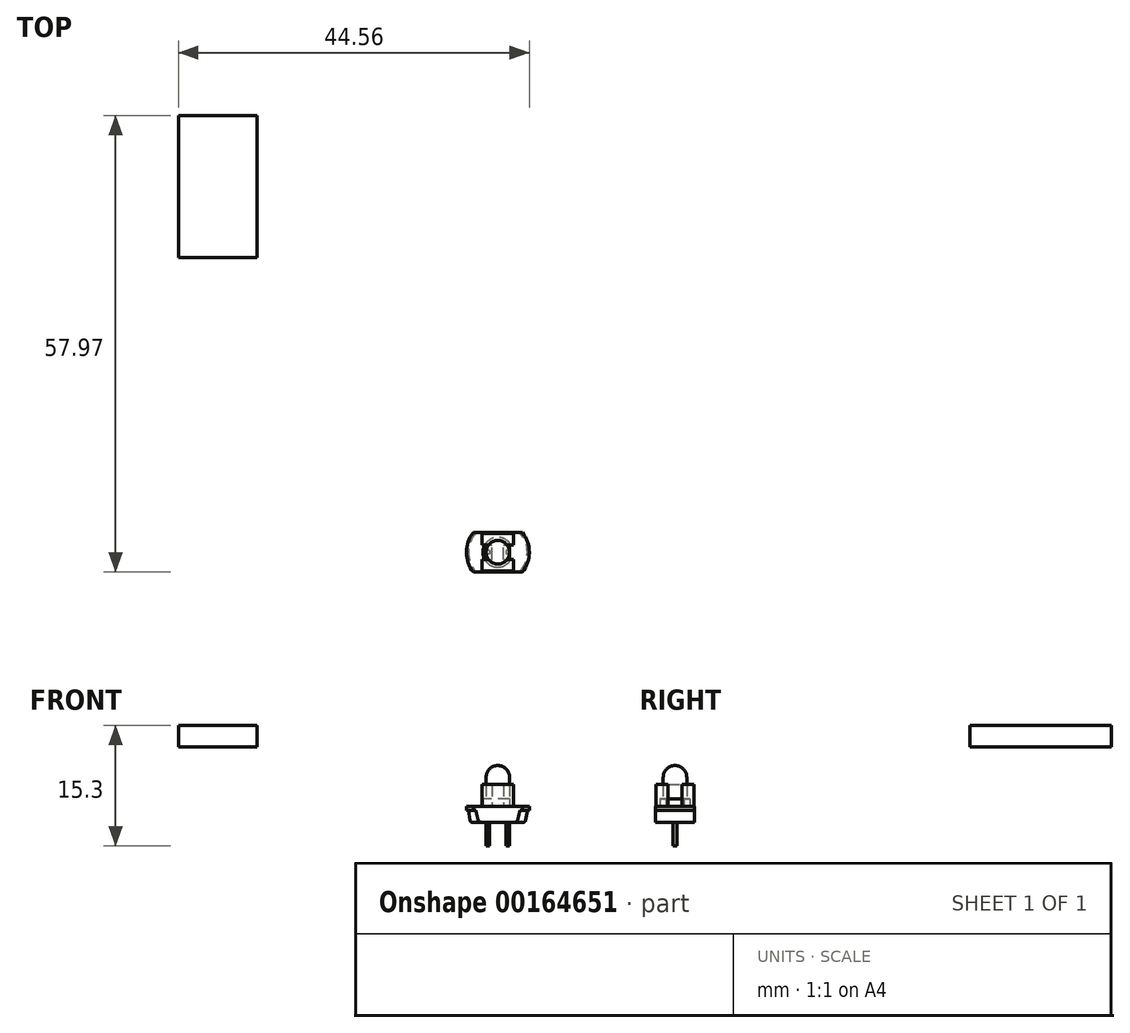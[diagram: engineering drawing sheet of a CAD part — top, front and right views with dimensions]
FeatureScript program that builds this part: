
annotation { "Feature Type Name" : "Feature", "Feature Type Description" : "" }
export const myFeature = defineFeature(function(context is Context, id is Id, definition is map)
    precondition{}
    {
        {
            var Q0;
            Q0=qCreatedBy(makeId("Front.planeOp"),FACE);
            var sketch = newSketch(context, id + "F0", { "sketchPlane" : qUnion([Q0])});
            skLineSegment(sketch, "E0", {"start": v(0, 10.98) * mm, "end": v(0, -8.22) * mm, "construction": true});
            skSolve(sketch);
        }
        {
            var Q0;
            Q0=qCreatedBy(makeId("Top.planeOp"),FACE);
            cPlane(context, id + "F1", {"entities" : qUnion([Q0]), "cplaneType" : CPlaneType.OFFSET, "offset" : 2 * mm, "width" : 150 * mm, "height" : 150 * mm});
        }
        {
            var Q0;
            Q0=qCreatedBy(makeId("Top.planeOp"),FACE);
            var sketch = newSketch(context, id + "F2", { "sketchPlane" : qUnion([Q0])});
            skLineSegment(sketch, "E1", {"start": v(0, 8.57) * mm, "end": v(0, -6.8) * mm, "construction": true});
            skLineSegment(sketch, "E2", {"start": v(-7.73, 0) * mm, "end": v(6.61, 0) * mm, "construction": true});
            skLineSegment(sketch, "E3.bottom", {"start": v(-4.25, 1.75) * mm, "end": v(4.25, 1.75) * mm});
            skLineSegment(sketch, "E3.top", {"start": v(-4.25, -1.75) * mm, "end": v(4.25, -1.75) * mm});
            skLineSegment(sketch, "E3.left", {"start": v(-4.25, 1.75) * mm, "end": v(-4.25, -1.75) * mm});
            skLineSegment(sketch, "E3.right", {"start": v(4.25, 1.75) * mm, "end": v(4.25, -1.75) * mm});
            skSolve(sketch);
        }
        {
            var Q0;
            Q0=qSketchRegion(id+"F2",true);
            extrude(context, id + "F3", {"entities" : qUnion([Q0]), "depth" : 3.5 * mm});
        }
        {
            var Q0;
            Q0=makeQuery(id+"F3.opExtrude","CAP_FACE",FACE,{"disambiguationData":[OSD([sQuery(id+"F2.wireOp",EDGE,"E3.bottom"),sQuery(id+"F2.wireOp",EDGE,"E3.top"),sQuery(id+"F2.wireOp",EDGE,"E3.left"),sQuery(id+"F2.wireOp",EDGE,"E3.right")])],"isStart":false});
            var sketch = newSketch(context, id + "F4", { "sketchPlane" : qUnion([Q0])});
            skLineSegment(sketch, "E4.bottom", {"start": v(-1.75, 0.75) * mm, "end": v(-0.25, 0.75) * mm});
            skLineSegment(sketch, "E4.top", {"start": v(-1.75, -0.75) * mm, "end": v(-0.25, -0.75) * mm});
            skLineSegment(sketch, "E4.left", {"start": v(-1.75, 0.75) * mm, "end": v(-1.75, -0.75) * mm});
            skLineSegment(sketch, "E4.right", {"start": v(-0.25, 0.75) * mm, "end": v(-0.25, -0.75) * mm});
            skLineSegment(sketch, "E5", {"start": v(-2.91, 0) * mm, "end": v(1.63, 0) * mm, "construction": true});
            skSolve(sketch);
        }
        {
            var Q0;
            Q0=qSketchRegion(id+"F4",true);
            extrude(context, id + "F5", {"entities" : qUnion([Q0]), "operationType" : NewBodyOperationType.ADD, "depth" : 2 * mm});
        }
        {
            var Q0;
            Q0=makeQuery(id+"F3.opExtrude","CAP_FACE",FACE,{"disambiguationData":[OSD([sQuery(id+"F2.wireOp",EDGE,"E3.bottom"),sQuery(id+"F2.wireOp",EDGE,"E3.top"),sQuery(id+"F2.wireOp",EDGE,"E3.left"),sQuery(id+"F2.wireOp",EDGE,"E3.right")])],"isStart":true});
            var sketch = newSketch(context, id + "F6", { "sketchPlane" : qUnion([Q0])});
            skLineSegment(sketch, "E6.bottom", {"start": v(-2.8, 2.5) * mm, "end": v(-2.2, 2.5) * mm});
            skLineSegment(sketch, "E6.top", {"start": v(-2.8, 1.75) * mm, "end": v(-2.2, 1.75) * mm});
            skLineSegment(sketch, "E6.left", {"start": v(-2.8, 2.5) * mm, "end": v(-2.8, 1.75) * mm});
            skLineSegment(sketch, "E6.right", {"start": v(-2.2, 2.5) * mm, "end": v(-2.2, 1.75) * mm});
            skLineSegment(sketch, "E7.1.0.0", {"start": v(-0.3, 1.75) * mm, "end": v(0.3, 1.75) * mm});
            skLineSegment(sketch, "E7.1.0.1", {"start": v(-0.3, 2.5) * mm, "end": v(-0.3, 1.75) * mm});
            skLineSegment(sketch, "E7.1.0.2", {"start": v(0.3, 2.5) * mm, "end": v(0.3, 1.75) * mm});
            skLineSegment(sketch, "E7.1.0.3", {"start": v(-0.3, 2.5) * mm, "end": v(0.3, 2.5) * mm});
            skLineSegment(sketch, "E7.2.0.0", {"start": v(2.2, 1.75) * mm, "end": v(2.8, 1.75) * mm});
            skLineSegment(sketch, "E7.2.0.1", {"start": v(2.2, 2.5) * mm, "end": v(2.2, 1.75) * mm});
            skLineSegment(sketch, "E7.2.0.2", {"start": v(2.8, 2.5) * mm, "end": v(2.8, 1.75) * mm});
            skLineSegment(sketch, "E7.2.0.3", {"start": v(2.2, 2.5) * mm, "end": v(2.8, 2.5) * mm});
            skLineSegment(sketch, "E7.direction1", {"start": v(-2.8, 1.75) * mm, "end": v(-0.3, 1.75) * mm, "construction": true});
            skLineSegment(sketch, "E8", {"start": v(-2.83, 0) * mm, "end": v(2.14, 0) * mm, "construction": true});
            skLineSegment(sketch, "E9.0.MirrorCS", {"start": v(2.2, -2.5) * mm, "end": v(2.8, -2.5) * mm});
            skLineSegment(sketch, "E9.1.MirrorCS", {"start": v(-0.3, -2.5) * mm, "end": v(0.3, -2.5) * mm});
            skLineSegment(sketch, "E9.2.MirrorCS", {"start": v(-2.8, -2.5) * mm, "end": v(-2.2, -2.5) * mm});
            skLineSegment(sketch, "E9.3.MirrorCS", {"start": v(2.8, -2.5) * mm, "end": v(2.8, -1.75) * mm});
            skLineSegment(sketch, "E9.4.MirrorCS", {"start": v(2.2, -2.5) * mm, "end": v(2.2, -1.75) * mm});
            skLineSegment(sketch, "E9.5.MirrorCS", {"start": v(0.3, -2.5) * mm, "end": v(0.3, -1.75) * mm});
            skLineSegment(sketch, "E9.6.MirrorCS", {"start": v(-0.3, -2.5) * mm, "end": v(-0.3, -1.75) * mm});
            skLineSegment(sketch, "E9.7.MirrorCS", {"start": v(-2.2, -2.5) * mm, "end": v(-2.2, -1.75) * mm});
            skLineSegment(sketch, "E9.8.MirrorCS", {"start": v(-2.8, -2.5) * mm, "end": v(-2.8, -1.75) * mm});
            skLineSegment(sketch, "E9.9.MirrorCS", {"start": v(2.2, -1.75) * mm, "end": v(2.8, -1.75) * mm});
            skLineSegment(sketch, "E9.10.MirrorCS", {"start": v(-2.8, -1.75) * mm, "end": v(-2.2, -1.75) * mm});
            skLineSegment(sketch, "E9.11.MirrorCS", {"start": v(-0.3, -1.75) * mm, "end": v(0.3, -1.75) * mm});
            skSolve(sketch);
        }
        {
            var Q0;
            Q0=qSketchRegion(id+"F6",true);
            extrude(context, id + "F7", {"entities" : qUnion([Q0]), "operationType" : NewBodyOperationType.ADD, "oppositeDirection" : true, "depth" : 0.3 * mm});
        }
        {
            var Q0;
            Q0=makeQuery(id+"F3.opExtrude","SWEPT_BODY",BODY,{"disambiguationData":[OSD([sQuery(id+"F2.wireOp",EDGE,"E3.bottom"),sQuery(id+"F2.wireOp",EDGE,"E3.top"),sQuery(id+"F2.wireOp",EDGE,"E3.left"),sQuery(id+"F2.wireOp",EDGE,"E3.right")])]});
            transform(context, id + "F8", {"entities" : qUnion([Q0]), "transformType" : TransformType.TRANSLATION_3D, "dx" : -23 * mm, "dy" : 46.3 * mm, "dz" : 7.6 * mm, "makeCopy" : false});
        }
        {
            var Q0;
            Q0=qCreatedBy(makeId("Front.planeOp"),FACE);
            var sketch = newSketch(context, id + "F9", { "sketchPlane" : qUnion([Q0])});
            skLineSegment(sketch, "E10", {"start": v(0, 0) * mm, "end": v(4, 0) * mm});
            skLineSegment(sketch, "E11", {"start": v(4, 0) * mm, "end": v(4, -0.5) * mm});
            skLineSegment(sketch, "E12", {"start": v(4, -0.5) * mm, "end": v(3.75, -0.5) * mm});
            skLineSegment(sketch, "E13", {"start": v(3.75, -0.5) * mm, "end": v(3.54, -1.75) * mm});
            skLineSegment(sketch, "E14", {"start": v(3.25, -2) * mm, "end": v(0, -2) * mm});
            skLineSegment(sketch, "E15", {"start": v(0, -2) * mm, "end": v(0, 0) * mm});
            skPoint(sketch, "E16.visualSharp", {"position": v(3.5, -2) * mm});
            skArc(sketch, "E16.filletArc", {"start": v(3.25, -2) * mm, "mid": v(3.44, -1.93) * mm, "end": v(3.54, -1.75) * mm});
            skSolve(sketch);
        }
        {
            var Q0;
            Q0=qSketchRegion(id+"F9",true);
            var Q1;
            Q1=sQuery(id+"F9.wireOp",EDGE,"E15");
            revolve(context, id + "F10", {"entities" : qUnion([Q0]), "axis" : qUnion([Q1]), "revolveType" : RevolveType.FULL});
        }
        {
            var Q0;
            Q0=qCreatedBy(makeId("Front.planeOp"),FACE);
            var sketch = newSketch(context, id + "F11", { "sketchPlane" : qUnion([Q0])});
            skLineSegment(sketch, "E17", {"start": v(0, 0) * mm, "end": v(4, 0) * mm});
            skLineSegment(sketch, "E18", {"start": v(4, 0) * mm, "end": v(4, -0.5) * mm});
            skLineSegment(sketch, "E19", {"start": v(4, -0.5) * mm, "end": v(3.75, -0.5) * mm});
            skLineSegment(sketch, "E20", {"start": v(3.75, -0.5) * mm, "end": v(3.64, -0.68) * mm});
            skLineSegment(sketch, "E21", {"start": v(0, 0) * mm, "end": v(0, -2) * mm});
            skLineSegment(sketch, "E22", {"start": v(0, -2) * mm, "end": v(0.5, -2) * mm});
            skArc(sketch, "E23", {"start": v(0.5, -2) * mm, "mid": v(2.2, -1.66) * mm, "end": v(3.64, -0.68) * mm});
            skSolve(sketch);
        }
        {
            var Q0;
            Q0=qSketchRegion(id+"F11",true);
            var Q1;
            Q1=sQuery(id+"F11.wireOp",EDGE,"E21");
            revolve(context, id + "F12", {"entities" : qUnion([Q0]), "axis" : qUnion([Q1]), "revolveType" : RevolveType.FULL});
        }
        {
            var Q0;
            Q0=makeQuery(id+"F12.opRevolve","SWEPT_BODY",BODY,{"disambiguationData":[OSD([sQuery(id+"F11.wireOp",EDGE,"E17"),sQuery(id+"F11.wireOp",EDGE,"E18"),sQuery(id+"F11.wireOp",EDGE,"E19"),sQuery(id+"F11.wireOp",EDGE,"E20"),sQuery(id+"F11.wireOp",EDGE,"E21"),sQuery(id+"F11.wireOp",EDGE,"E22"),sQuery(id+"F11.wireOp",EDGE,"E23")])]});
            transform(context, id + "F13", {"entities" : qUnion([Q0]), "transformType" : TransformType.COPY});
        }
        {
            var Q0;
            Q0=makeQuery(id+"F13.opPattern","COPY",FACE,{"derivedFrom":makeQuery(id+"F12.opRevolve","SWEPT_FACE",FACE,{"disambiguationData":[OSD([sQuery(id+"F11.wireOp",EDGE,"E17")])]}),"instanceName":"1"});
            var sketch = newSketch(context, id + "F14", { "sketchPlane" : qUnion([Q0])});
            skLineSegment(sketch, "E24", {"start": v(-3.12, 2.5) * mm, "end": v(3.12, 2.5) * mm});
            skLineSegment(sketch, "E25", {"start": v(-3.12, -2.5) * mm, "end": v(3.12, -2.5) * mm});
            skLineSegment(sketch, "E26", {"start": v(0, 0) * mm, "end": v(3.07, 0) * mm, "construction": true});
            skArc(sketch, "E27.0", {"start": v(-3.12, 2.5) * mm, "mid": v(-4, 0) * mm, "end": v(-3.12, -2.5) * mm});
            skArc(sketch, "E28.trimOffspring", {"start": v(3.12, -2.5) * mm, "mid": v(4, 0) * mm, "end": v(3.12, 2.5) * mm});
            skSolve(sketch);
        }
        {
            var Q0;
            Q0=qSketchRegion(id+"F14",true);
            extrude(context, id + "F15", {"entities" : qUnion([Q0]), "operationType" : NewBodyOperationType.INTERSECT, "oppositeDirection" : true, "depth" : 25 * mm});
        }
        {
            var Q0;
            Q0=qCreatedBy(makeId("Front.planeOp"),FACE);
            var sketch = newSketch(context, id + "F16", { "sketchPlane" : qUnion([Q0])});
            skLineSegment(sketch, "E29", {"start": v(0, 0) * mm, "end": v(0, 5.2) * mm});
            skLineSegment(sketch, "E30", {"start": v(0, 0) * mm, "end": v(1.9, 0) * mm});
            skLineSegment(sketch, "E31", {"start": v(1.9, 0) * mm, "end": v(1.9, 1) * mm});
            skLineSegment(sketch, "E32", {"start": v(1.9, 1) * mm, "end": v(1.5, 1) * mm});
            skLineSegment(sketch, "E33", {"start": v(1.5, 1) * mm, "end": v(1.5, 3.7) * mm});
            skArc(sketch, "E34", {"start": v(1.5, 3.7) * mm, "mid": v(1.06, 4.76) * mm, "end": v(0, 5.2) * mm});
            skLineSegment(sketch, "E35", {"start": v(0, 3.7) * mm, "end": v(1, 3.7) * mm, "construction": true});
            skSolve(sketch);
        }
        {
            var Q0;
            Q0=qSketchRegion(id+"F16",true);
            var Q1;
            Q1=sQuery(id+"F16.wireOp",EDGE,"E29");
            revolve(context, id + "F17", {"entities" : qUnion([Q0]), "axis" : qUnion([Q1]), "revolveType" : RevolveType.FULL});
        }
        {
            var Q0;
            Q0=makeQuery(id+"F17.opRevolve","SWEPT_FACE",FACE,{"disambiguationData":[OSD([sQuery(id+"F16.wireOp",EDGE,"E30")])]});
            var sketch = newSketch(context, id + "F18", { "sketchPlane" : qUnion([Q0])});
            skLineSegment(sketch, "E36.bottom", {"start": v(2.77, -2.04) * mm, "end": v(1.5, -2.04) * mm});
            skLineSegment(sketch, "E36.top", {"start": v(2.77, 2.1) * mm, "end": v(1.5, 2.1) * mm});
            skLineSegment(sketch, "E36.left", {"start": v(2.77, -2.04) * mm, "end": v(2.77, 2.1) * mm});
            skLineSegment(sketch, "E36.right", {"start": v(1.5, -2.04) * mm, "end": v(1.5, 2.1) * mm});
            skSolve(sketch);
        }
        {
            var Q0;
            Q0=qSketchRegion(id+"F18",true);
            extrude(context, id + "F19", {"entities" : qUnion([Q0]), "operationType" : NewBodyOperationType.REMOVE, "oppositeDirection" : true, "depth" : 25 * mm});
        }
        {
            var Q0;
            Q0=makeQuery(id+"F17.opRevolve","SWEPT_FACE",FACE,{"disambiguationData":[OSD([sQuery(id+"F16.wireOp",EDGE,"E30")])]});
            var sketch = newSketch(context, id + "F20", { "sketchPlane" : qUnion([Q0])});
            skLineSegment(sketch, "E37.bottom", {"start": v(-1.05, -0.23) * mm, "end": v(-1.5, -0.22) * mm});
            skLineSegment(sketch, "E37.top", {"start": v(-1.05, 0.23) * mm, "end": v(-1.5, 0.23) * mm});
            skLineSegment(sketch, "E37.left", {"start": v(-1.05, -0.23) * mm, "end": v(-1.05, 0.23) * mm});
            skLineSegment(sketch, "E37.right", {"start": v(-1.5, -0.22) * mm, "end": v(-1.5, 0.23) * mm});
            skPoint(sketch, "E37.middle", {"position": v(-1.27, 0) * mm});
            skLineSegment(sketch, "E38.bottom", {"start": v(1.5, -0.22) * mm, "end": v(1.04, -0.23) * mm});
            skLineSegment(sketch, "E38.top", {"start": v(1.5, 0.23) * mm, "end": v(1.04, 0.23) * mm});
            skLineSegment(sketch, "E38.left", {"start": v(1.5, -0.22) * mm, "end": v(1.5, 0.23) * mm});
            skLineSegment(sketch, "E38.right", {"start": v(1.04, -0.23) * mm, "end": v(1.04, 0.23) * mm});
            skPoint(sketch, "E38.middle", {"position": v(1.27, 0) * mm});
            skSolve(sketch);
        }
        {
            var Q0;
            Q0=qSketchRegion(id+"F20",true);
            extrude(context, id + "F21", {"entities" : qUnion([Q0]), "operationType" : NewBodyOperationType.ADD, "depth" : 5 * mm});
        }
        {
            var Q0;
            Q0=qCreatedBy(makeId("Top.planeOp"),FACE);
            var sketch = newSketch(context, id + "F22", { "sketchPlane" : qUnion([Q0])});
            skLineSegment(sketch, "E39.bottom", {"start": v(-5, 0) * mm, "end": v(5, 0) * mm});
            skLineSegment(sketch, "E39.top", {"start": v(-5, 18) * mm, "end": v(5, 18) * mm});
            skLineSegment(sketch, "E39.left", {"start": v(-5, 0) * mm, "end": v(-5, 18) * mm});
            skLineSegment(sketch, "E39.right", {"start": v(5, 0) * mm, "end": v(5, 18) * mm});
            skPoint(sketch, "E40", {"position": v(0, 0) * mm});
            skSolve(sketch);
        }
        {
            var Q0;
            Q0=qSketchRegion(id+"F22",true);
            extrude(context, id + "F23", {"entities" : qUnion([Q0]), "depth" : 2.7 * mm});
        }
        {
            var Q0;
            Q0=makeQuery(id+"F23.opExtrude","SWEPT_BODY",BODY,{"disambiguationData":[OSD([sQuery(id+"F22.wireOp",EDGE,"E39.bottom"),sQuery(id+"F22.wireOp",EDGE,"E39.top"),sQuery(id+"F22.wireOp",EDGE,"E39.left"),sQuery(id+"F22.wireOp",EDGE,"E39.right")])]});
            transform(context, id + "F24", {"entities" : qUnion([Q0]), "transformType" : TransformType.TRANSLATION_3D, "dx" : -35.56 * mm, "dy" : 37.47 * mm, "dz" : 7.6 * mm, "makeCopy" : false});
        }
        {
            var Q0;
            Q0=qCreatedBy(makeId("Top.planeOp"),FACE);
            var sketch = newSketch(context, id + "F25", { "sketchPlane" : qUnion([Q0])});
            skLineSegment(sketch, "E41.bottom", {"start": v(-0.75, -2.4) * mm, "end": v(0.75, -2.4) * mm});
            skLineSegment(sketch, "E41.top", {"start": v(-0.75, 2.4) * mm, "end": v(0.75, 2.4) * mm});
            skLineSegment(sketch, "E41.left", {"start": v(-0.75, -2.4) * mm, "end": v(-0.75, 2.4) * mm});
            skLineSegment(sketch, "E41.right", {"start": v(0.75, -2.4) * mm, "end": v(0.75, 2.4) * mm});
            skLineSegment(sketch, "E42.bottom", {"start": v(-2, -0.9) * mm, "end": v(2, -0.9) * mm});
            skLineSegment(sketch, "E42.top", {"start": v(-2, -2.4) * mm, "end": v(2, -2.4) * mm});
            skLineSegment(sketch, "E42.left", {"start": v(-2, -0.9) * mm, "end": v(-2, -2.4) * mm});
            skLineSegment(sketch, "E42.right", {"start": v(2, -0.9) * mm, "end": v(2, -2.4) * mm});
            skLineSegment(sketch, "E43.bottom", {"start": v(-2, 2.4) * mm, "end": v(2, 2.4) * mm});
            skLineSegment(sketch, "E43.top", {"start": v(-2, 0.9) * mm, "end": v(2, 0.9) * mm});
            skLineSegment(sketch, "E43.left", {"start": v(-2, 2.4) * mm, "end": v(-2, 0.9) * mm});
            skLineSegment(sketch, "E43.right", {"start": v(2, 2.4) * mm, "end": v(2, 0.9) * mm});
            skPoint(sketch, "E44", {"position": v(0, -2.4) * mm});
            skSolve(sketch);
        }
        {
            var Q0;
            Q0=qSketchRegion(id+"F25",true);
            extrude(context, id + "F26", {"entities" : qUnion([Q0]), "depth" : 2.8 * mm});
        }
    });
